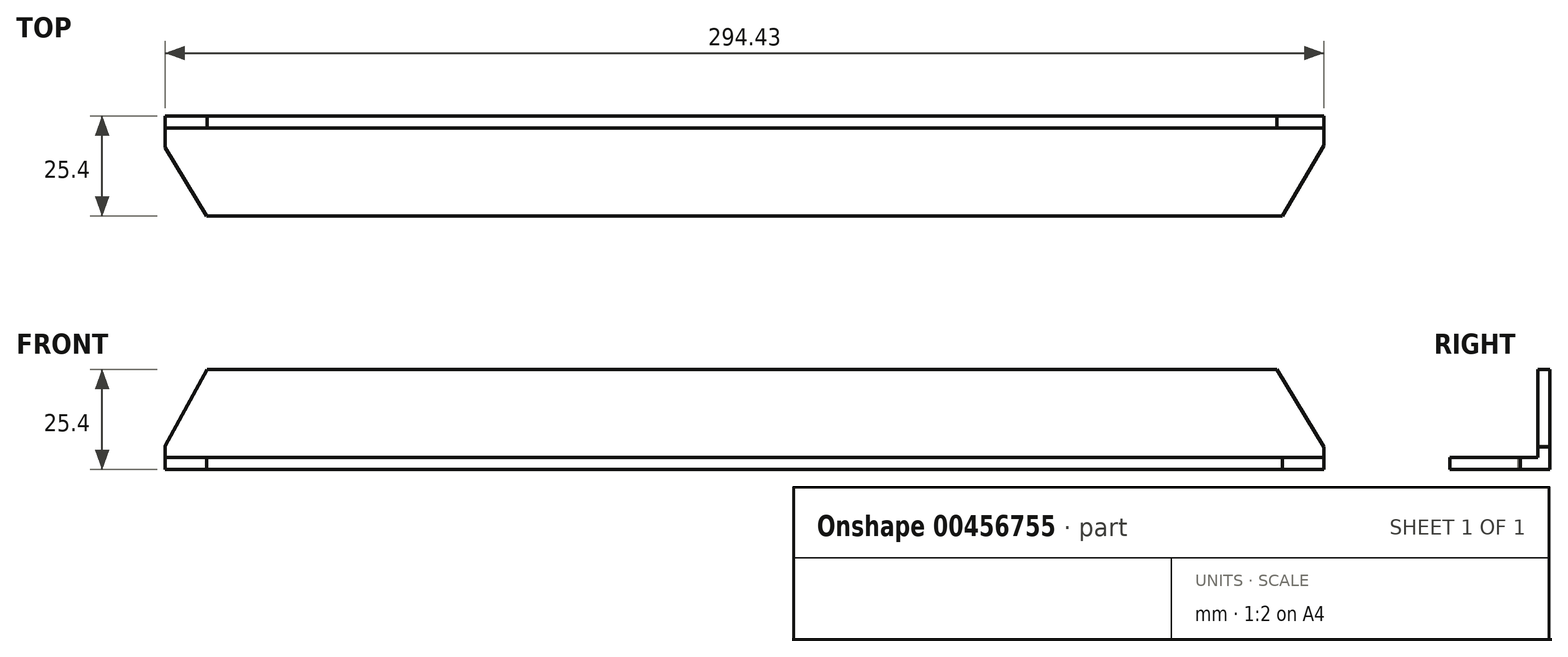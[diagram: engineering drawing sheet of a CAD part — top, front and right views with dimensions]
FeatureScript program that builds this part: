
annotation { "Feature Type Name" : "Feature", "Feature Type Description" : "" }
export const myFeature = defineFeature(function(context is Context, id is Id, definition is map)
    precondition{}
    {
        {
            var Q0;
            Q0=qCreatedBy(makeId("Front.planeOp"),FACE);
            var sketch = newSketch(context, id + "F0", { "sketchPlane" : qUnion([Q0])});
            skLineSegment(sketch, "E0.bottom", {"start": v(0, 0) * mm, "end": v(294.43, 0) * mm});
            skLineSegment(sketch, "E0.top", {"start": v(0, 25.4) * mm, "end": v(294.43, 25.4) * mm});
            skLineSegment(sketch, "E0.left", {"start": v(0, 0) * mm, "end": v(0, 25.4) * mm});
            skLineSegment(sketch, "E0.right", {"start": v(294.43, 0) * mm, "end": v(294.43, 25.4) * mm});
            skSolve(sketch);
        }
        {
            var Q0;
            Q0=makeQuery(id+"F0.imprint","IMPRINT",FACE,{"disambiguationData":[TD([[makeQuery(id+"F0.imprint","IMPRINT",EDGE,{"derivedFrom":sQuery(id+"F0.wireOp",EDGE,"E0.bottom")}),1.0]])]});
            extrude(context, id + "F1", {"entities" : qUnion([Q0]), "depth" : 3.05 * mm});
        }
        {
            var Q0;
            Q0=makeQuery(id+"F1.opExtrude","CAP_FACE",FACE,{"disambiguationData":[OSD([sQuery(id+"F0.wireOp",EDGE,"E0.bottom"),sQuery(id+"F0.wireOp",EDGE,"E0.top"),sQuery(id+"F0.wireOp",EDGE,"E0.left"),sQuery(id+"F0.wireOp",EDGE,"E0.right")])],"isStart":false});
            var sketch = newSketch(context, id + "F2", { "sketchPlane" : qUnion([Q0])});
            skLineSegment(sketch, "E1.bottom", {"start": v(294.43, 0) * mm, "end": v(0, 0) * mm});
            skLineSegment(sketch, "E1.top", {"start": v(294.43, 3.05) * mm, "end": v(0, 3.05) * mm});
            skLineSegment(sketch, "E1.left", {"start": v(294.43, 0) * mm, "end": v(294.43, 3.05) * mm});
            skLineSegment(sketch, "E1.right", {"start": v(0, 0) * mm, "end": v(0, 3.05) * mm});
            skSolve(sketch);
        }
        {
            var Q0;
            Q0=makeQuery(id+"F2.imprint","IMPRINT",FACE,{"disambiguationData":[TD([[makeQuery(id+"F2.imprint","IMPRINT",EDGE,{"derivedFrom":sQuery(id+"F2.wireOp",EDGE,"E1.bottom")}),1.0]])]});
            extrude(context, id + "F3", {"entities" : qUnion([Q0]), "operationType" : NewBodyOperationType.ADD, "depth" : 22.35 * mm});
        }
        {
            var Q0;
            Q0=makeQuery(id+"F1.opExtrude","CAP_FACE",FACE,{"disambiguationData":[OSD([sQuery(id+"F0.wireOp",EDGE,"E0.bottom"),sQuery(id+"F0.wireOp",EDGE,"E0.top"),sQuery(id+"F0.wireOp",EDGE,"E0.left"),sQuery(id+"F0.wireOp",EDGE,"E0.right")])],"isStart":false});
            var sketch = newSketch(context, id + "F4", { "sketchPlane" : qUnion([Q0])});
            skLineSegment(sketch, "E2", {"start": v(10.68, 25.4) * mm, "end": v(0, 5.93) * mm});
            skLineSegment(sketch, "E3", {"start": v(0, 5.93) * mm, "end": v(-15.1, 25.4) * mm});
            skLineSegment(sketch, "E4", {"start": v(-15.1, 25.4) * mm, "end": v(4.4, 35.48) * mm});
            skLineSegment(sketch, "E5", {"start": v(4.4, 35.48) * mm, "end": v(10.68, 25.4) * mm});
            skSolve(sketch);
        }
        {
            var Q0;
            Q0 = qSketchRegion(id + "F4", true);
            extrude(context, id + "F5", {"entities" : qUnion([Q0]), "operationType" : NewBodyOperationType.REMOVE, "oppositeDirection" : true, "depth" : 25.4 * mm});
        }
        {
            var Q0;
            Q0=makeQuery(id+"F3.opExtrude","SWEPT_FACE",FACE,{"disambiguationData":[OSD([sQuery(id+"F2.wireOp",EDGE,"E1.top")])]});
            var sketch = newSketch(context, id + "F6", { "sketchPlane" : qUnion([Q0])});
            skLineSegment(sketch, "E6", {"start": v(0, -8.05) * mm, "end": v(13.45, -30.06) * mm});
            skLineSegment(sketch, "E7", {"start": v(13.45, -30.06) * mm, "end": v(9.96, -44.27) * mm});
            skLineSegment(sketch, "E8", {"start": v(9.96, -44.27) * mm, "end": v(-4.95, -25.4) * mm});
            skLineSegment(sketch, "E9", {"start": v(-4.95, -25.4) * mm, "end": v(0, -8.05) * mm});
            skSolve(sketch);
        }
        {
            var Q0;
            Q0 = qSketchRegion(id + "F6", true);
            extrude(context, id + "F7", {"entities" : qUnion([Q0]), "operationType" : NewBodyOperationType.REMOVE, "oppositeDirection" : true, "depth" : 25.4 * mm});
        }
        {
            var Q0;
            Q0=makeQuery(id+"F3.opExtrude","SWEPT_FACE",FACE,{"disambiguationData":[OSD([sQuery(id+"F2.wireOp",EDGE,"E1.top")])]});
            var sketch = newSketch(context, id + "F8", { "sketchPlane" : qUnion([Q0])});
            skLineSegment(sketch, "E10", {"start": v(294.43, -7.47) * mm, "end": v(280.86, -30.61) * mm});
            skLineSegment(sketch, "E11", {"start": v(280.86, -30.61) * mm, "end": v(297.75, -36.44) * mm});
            skLineSegment(sketch, "E12", {"start": v(297.75, -36.44) * mm, "end": v(299.84, 0) * mm});
            skLineSegment(sketch, "E13", {"start": v(299.84, 0) * mm, "end": v(294.43, -7.47) * mm});
            skSolve(sketch);
        }
        {
            var Q0;
            Q0 = qSketchRegion(id + "F8", true);
            extrude(context, id + "F9", {"entities" : qUnion([Q0]), "operationType" : NewBodyOperationType.REMOVE, "oppositeDirection" : true, "depth" : 25.4 * mm});
        }
        {
            var Q0;
            Q0=makeQuery(id+"F1.opExtrude","CAP_FACE",FACE,{"disambiguationData":[OSD([sQuery(id+"F0.wireOp",EDGE,"E0.bottom"),sQuery(id+"F0.wireOp",EDGE,"E0.top"),sQuery(id+"F0.wireOp",EDGE,"E0.left"),sQuery(id+"F0.wireOp",EDGE,"E0.right")])],"isStart":false});
            var sketch = newSketch(context, id + "F10", { "sketchPlane" : qUnion([Q0])});
            skLineSegment(sketch, "E14", {"start": v(294.43, 5.7) * mm, "end": v(279.36, 30.4) * mm});
            skLineSegment(sketch, "E15", {"start": v(279.36, 30.4) * mm, "end": v(311.67, 34.47) * mm});
            skLineSegment(sketch, "E16", {"start": v(311.67, 34.47) * mm, "end": v(301.66, 3.05) * mm});
            skLineSegment(sketch, "E17", {"start": v(301.66, 3.05) * mm, "end": v(294.43, 5.7) * mm});
            skSolve(sketch);
        }
        {
            var Q0;
            Q0 = qSketchRegion(id + "F10", true);
            extrude(context, id + "F11", {"entities" : qUnion([Q0]), "operationType" : NewBodyOperationType.REMOVE, "oppositeDirection" : true, "depth" : 25.4 * mm});
        }
    });
